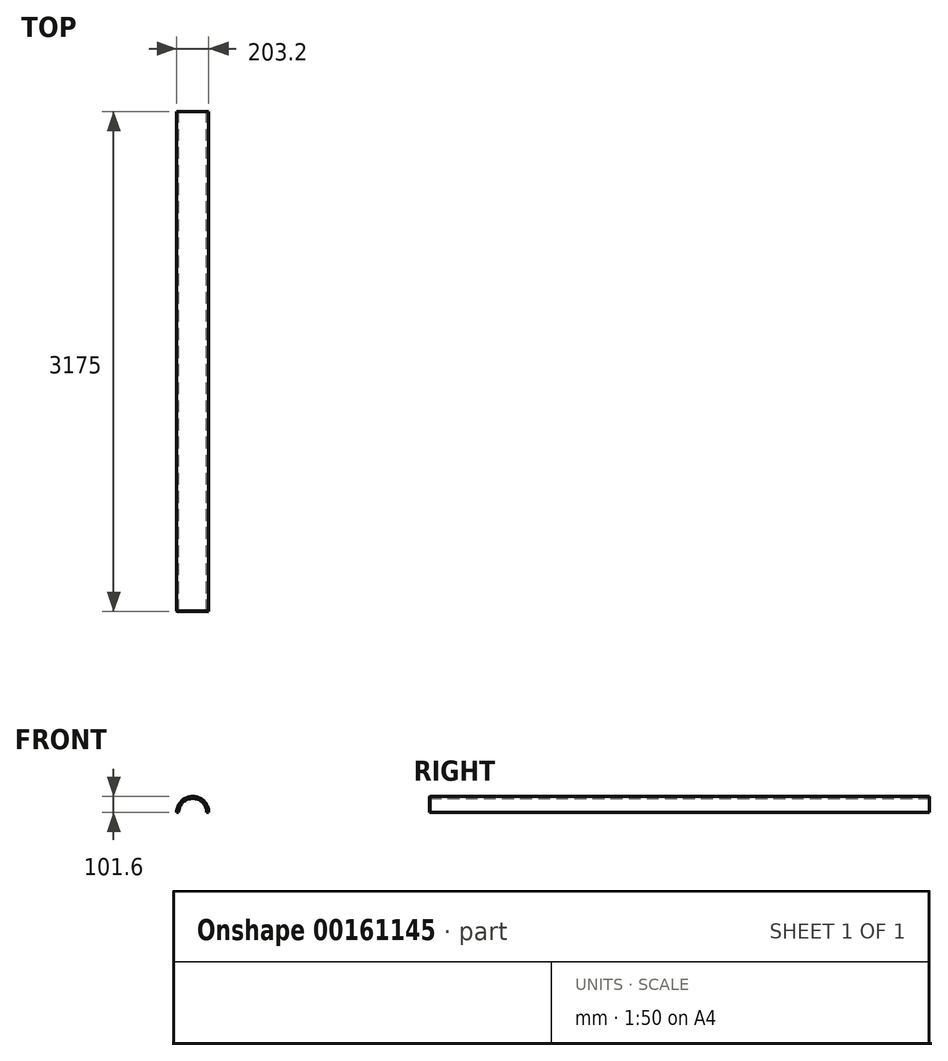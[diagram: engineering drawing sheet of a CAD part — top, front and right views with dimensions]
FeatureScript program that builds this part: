
annotation { "Feature Type Name" : "Feature", "Feature Type Description" : "" }
export const myFeature = defineFeature(function(context is Context, id is Id, definition is map)
    precondition{}
    {
        {
            var Q0;
            Q0=qCreatedBy(makeId("Front.planeOp"),FACE);
            var sketch = newSketch(context, id + "F0", { "sketchPlane" : qUnion([Q0])});
            skArc(sketch, "E0", {"start": v(103.65, 0) * mm, "mid": v(2.05, 101.6) * mm, "end": v(-99.55, 0) * mm});
            skArc(sketch, "E1", {"start": v(90.95, 0) * mm, "mid": v(2.05, 88.9) * mm, "end": v(-86.85, 0) * mm});
            skLineSegment(sketch, "E2", {"start": v(-99.55, 0) * mm, "end": v(-86.85, 0) * mm});
            skLineSegment(sketch, "E3.trimOffspring", {"start": v(90.95, 0) * mm, "end": v(103.65, 0) * mm});
            skPoint(sketch, "E4.orphan", {"position": v(-112.48, 0) * mm});
            skSolve(sketch);
        }
        {
            var Q0;
            Q0=qSketchRegion(id+"F0",true);
            extrude(context, id + "F1", {"entities" : qUnion([Q0]), "depth" : 3175 * mm});
        }
        {
            var Q0;
            Q0=makeQuery(id+"F1.opExtrude","CAP_EDGE",EDGE,{"disambiguationData":[OSD([sQuery(id+"F0.wireOp",EDGE,"E0")])],"isStart":true});
            var Q1;
            Q1=makeQuery(id+"F1.opExtrude","CAP_EDGE",EDGE,{"disambiguationData":[OSD([sQuery(id+"F0.wireOp",EDGE,"E0")])],"isStart":false});
            chamfer(context, id + "F2", {"entities" : qUnion([Q0, Q1]), "width" : 1.78 * mm, "tangentPropagation" : true});
        }
    });
